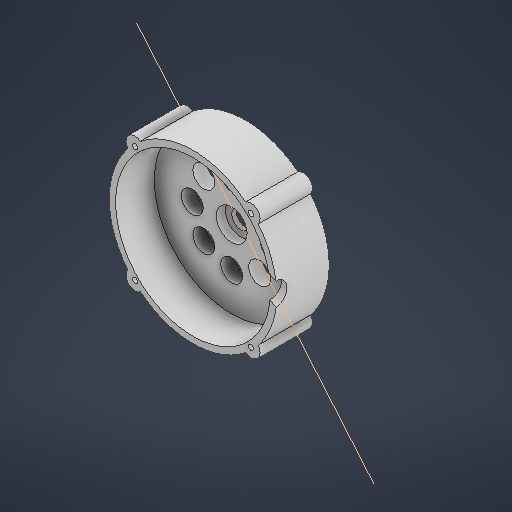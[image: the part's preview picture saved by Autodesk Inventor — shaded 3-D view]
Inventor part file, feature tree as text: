
AUTODESK INVENTOR PART (.ipt)
format: ipt  version: 2025.3 (Build 293356030, 356C)  size: 303,104 bytes
history: native  units: mm
features: sketch x7, extrude x5, plane x2, other x1
ambient origin geometry x8: Origin, YZ Plane, XZ Plane, XY Plane, X Axis, Y Axis, Z Axis, Center Point
bodies: Solid1 (feature_tree)
feature tree (15):
  sketch  "Sketch1"  dims[d1=40.0mm]
  extrude  "Extrusion1"  Depth=2.5mm TaperAngle=0.0deg
  extrude  "Extrusion2"  Depth=7.5mm TaperAngle=0.0deg
  extrude  "Extrusion3"  [1 undecoded]
  sketch  "Sketch2"  dims[d12=7.5mm d13=0.0mm d14=28.75mm d15=0.0mm]
  plane  "Work Plane1"
  sketch  "Sketch3"  dims[d18=10.65mm d19=30.0mm d20=0.0mm]
  plane  "Work Plane2"
  extrude  "Extrusion4"  Depth=30.0mm TaperAngle=0.0deg
  other  "Work Axis1"
  extrude  "Extrusion5"  Depth=21.65mm
  sketch  "Sketch Circular Pattern1"  dims[d2=10.0mm d3=16.9mm d4=85.0mm d5=90.0mm d6=2.9mm d7=5.0mm d8=360.0deg d9=92.0mm d10=2.5mm d11=0.0mm]
  sketch  "Sketch4"  dims[d21=12.0mm d22=21.65mm]
  sketch  "Sketch5"  dims[d23=80.0mm d25=360.0deg d27=0.0mm d28=0.0mm]
  sketch  "Sketch Circular Pattern2"  dims[d16=-13.089969mm d17=-5.235988mm]
note: 1 required parameter value undecoded (feature->parameter linkage not recoverable at this tier; creation-order binding heuristic only, values carry confidence <= 0.55)
